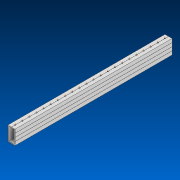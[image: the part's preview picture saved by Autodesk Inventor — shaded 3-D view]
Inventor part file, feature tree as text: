
AUTODESK INVENTOR PART (.ipt)
format: ipt  version: 2022.2 (Build 262287000, 287)  size: 484,864 bytes
history: native  units: in
note: dims shown in document units (in); Inventor stores cm internally (conversion verified against a paired STEP export)
features: other x23, extrude x1, pattern_linear x1, sketch x1
ambient origin geometry x8: Origin, YZ Plane, XZ Plane, XY Plane, X Axis, Y Axis, Z Axis, Center Point
bodies: Solid1 (feature_tree)
feature tree (26):
  extrude  "Extrusion1"  Depth=2.0in
  other  "Work Axis1"
  pattern_linear  "Rectangular Pattern1"  Spacing1=37.0in  [1 undecoded]
  sketch  "Sketch1"  dims[d0=1.0in d1=2.0in d2=37.0in d3=0.0in d4=8.6614in d6=1.0in]
  other  "Work Axis2"
  other  "Work Axis3"
  other  "Work Axis4"
  other  "Work Axis5"
  other  "Work Axis6"
  other  "Work Axis7"
  other  "Work Axis8"
  other  "Work Axis9"
  other  "Work Axis10"
  other  "Work Axis60"
  other  "Work Axis61"
  other  "Work Axis62"
  other  "Work Axis63"
  other  "Work Axis64"
  other  "Work Axis65"
  other  "Work Axis66"
  other  "Work Axis67"
  other  "Work Axis68"
  other  "Work Axis69"
  other  "Work Axis70"
  other  "Work Axis71"
  other  "Cut-Extrude2"
note: 1 required parameter value undecoded (feature->parameter linkage not recoverable at this tier; creation-order binding heuristic only, values carry confidence <= 0.55)
